FCSTD DOCUMENT  (FreeCAD 1.0R38641 +678 (Git))
Label: harnais_boucles
License: All rights reserved
LicenseURL: https://en.wikipedia.org/wiki/All_rights_reserved
objects: Sketcher::SketchObject×1, PartDesign::Body×1, App::Part×1
note: 3 computed .brp shape members not serialized (recipe doc carries the construction recipe); baked Part::Feature solids carry a one-line shape summary decoded from their .brp

FEATURE [Sketcher::SketchObject] Sketch
  ArcFitTolerance = 1e-06
  AttachmentSupport = -> [XY_Plane001]
  FullyConstrained = false
  MakeInternals = false
  MapMode = 5
  sketch-geometry (23):
    g0: LineSegment StartX=-12 StartY=-5 StartZ=0 EndX=-12 EndY=-7 EndZ=0
    g1: LineSegment StartX=-12 StartY=-7 StartZ=0 EndX=12 EndY=-7 EndZ=0
    g2: LineSegment StartX=12 StartY=-7 StartZ=0 EndX=12 EndY=-5 EndZ=0
    g3: LineSegment StartX=12 StartY=-5 StartZ=0 EndX=-12 EndY=-5 EndZ=0
    g4: LineSegment StartX=-23.2157 StartY=1.41421 StartZ=0 EndX=-6.24515 EndY=18.3848 EndZ=0
    g5: LineSegment StartX=-6.24515 StartY=18.3848 StartZ=0 EndX=-4.83094 EndY=16.9706 EndZ=0
    g6: LineSegment StartX=-4.83094 StartY=16.9706 StartZ=0 EndX=-21.8015 EndY=0 EndZ=0
    g7: LineSegment StartX=-21.8015 StartY=0 StartZ=0 EndX=-23.2157 EndY=1.41421 EndZ=0
    g8: LineSegment StartX=1.58328 StartY=23.3848 StartZ=0 EndX=18.5538 EndY=6.41421 EndZ=0
    g9: LineSegment StartX=18.5538 StartY=6.41421 StartZ=0 EndX=17.1396 EndY=5 EndZ=0
    g10: LineSegment StartX=17.1396 StartY=5 StartZ=0 EndX=0.169062 EndY=21.9706 EndZ=0
    g11: LineSegment StartX=0.169062 StartY=21.9706 StartZ=0 EndX=1.58328 EndY=23.3848 EndZ=0
    g12: GeomPoint X=0 Y=-5 Z=0
    g13: ArcOfCircle CenterX=0 CenterY=24.7203 CenterZ=0 NormalX=0 NormalY=0 NormalZ=1 AngleXU=0 Radius=2 StartAngle=0.581313 EndAngle=2.49144
    g14: ArcOfCircle CenterX=18.5538 CenterY=6.41421 CenterZ=0 NormalX=0 NormalY=0 NormalZ=1 AngleXU=0 Radius=2 StartAngle=5.82872 EndAngle=6.53823
    g15: ArcOfCircle CenterX=12 CenterY=-7 CenterZ=0 NormalX=0 NormalY=0 NormalZ=1 AngleXU=0 Radius=2 StartAngle=4.71239 EndAngle=5.82872
    g16: LineSegment StartX=13.797 StartY=-7.87796 StartZ=0 EndX=20.3508 EndY=5.53625 EndZ=0
    g17: LineSegment StartX=12 StartY=-9 StartZ=0 EndX=-12 EndY=-9 EndZ=0
    g18: LineSegment StartX=1.67149 StartY=25.8185 StartZ=0 EndX=20.4891 EndY=6.91879 EndZ=0
    g19: LineSegment StartX=-1.59199 StartY=25.9309 StartZ=0 EndX=-24.6319 EndY=2.82645 EndZ=0
    g20: ArcOfCircle CenterX=-23.2157 CenterY=1.41421 CenterZ=0 NormalX=0 NormalY=0 NormalZ=1 AngleXU=0 Radius=2 StartAngle=2.35759 EndAngle=4.06875
    g21: ArcOfCircle CenterX=-12 CenterY=-7 CenterZ=0 NormalX=0 NormalY=0 NormalZ=1 AngleXU=0 Radius=2 StartAngle=4.06875 EndAngle=4.71239
    g22: LineSegment StartX=-24.4159 StartY=-0.18562 StartZ=0 EndX=-13.2002 EndY=-8.59983 EndZ=0
  constraints (56):
    c: Coincident(g0,g1)
    c: Coincident(g1,g2)
    c: Coincident(g2,g3)
    c: Coincident(g3,g0)
    c: Vertical(g0)
    c: Vertical(g2)
    c: Horizontal(g1)
    c: Horizontal(g3)
    c: Distance(g0,g2) = 24
    c: Distance(g1,g3) = 2
    c: Coincident(g5,g4)
    c: Coincident(g6,g5)
    c: Coincident(g7,g6)
    c: Coincident(g7,g4)
    c: Perpendicular(g6,g7)
    c: Perpendicular(g5,g4)
    c: Perpendicular(g5,g6)
    c: Equal(g6,g3)
    c: Equal(g7,g0)
    c: Coincident(g8,g9)
    c: Coincident(g9,g10)
    c: Coincident(g10,g11)
    c: Coincident(g11,g8)
    c: Parallel(g11,g9)
    c: Parallel(g10,g8)
    c: Perpendicular(g10,g11)
    c: Perpendicular(g10,g6)
    c: Equal(g11,g2)
    c: Equal(g3,g10)
    c: Angle(g6,g-2) = 0.785398
    c: Distance(g-1,g3) = 5
    c: Symmetric(g3,g3,g12)
    c: PointOnObject(g12,g-2)
    c: DistanceX(g5,g10) = 5
    c: PointOnObject(g6,g-1)
    c: Distance(g9,g-1) = 5
    c: PointOnObject(g13,g-2)
    c: Horizontal(g17)
    c: Tangent(g16,g15) = -1.5708
    c: Tangent(g17,g15) = 1.5708
    c: Tangent(g16,g14) = -1.5708
    c: Distance(g1,g17) = 2
    c: Coincident(g15,g1)
    c: Coincident(g14,g8)
    c: Coincident(g18,g13)
    c: Coincident(g18,g14)
    c: Coincident(g19,g13)
    c: Coincident(g20,g4)
    c: Coincident(g21,g0)
    c: Tangent(g22,g21) = -1.5708
    c: Tangent(g20,g22) = -1.5708
    c: Tangent(g20,g19) = -1.5708
    c: Tangent(g21,g17) = 1.5708
    c: Equal(g14,g13)
    c: Equal(g13,g20)
    c: Equal(g20,g21)
FEATURE [PartDesign::Body] Body
  AllowCompound = false
  Group = -> [Sketch]
  Origin = -> Origin001
FEATURE [App::Part] Part
  Group = -> [Body]
  Origin = -> Origin
